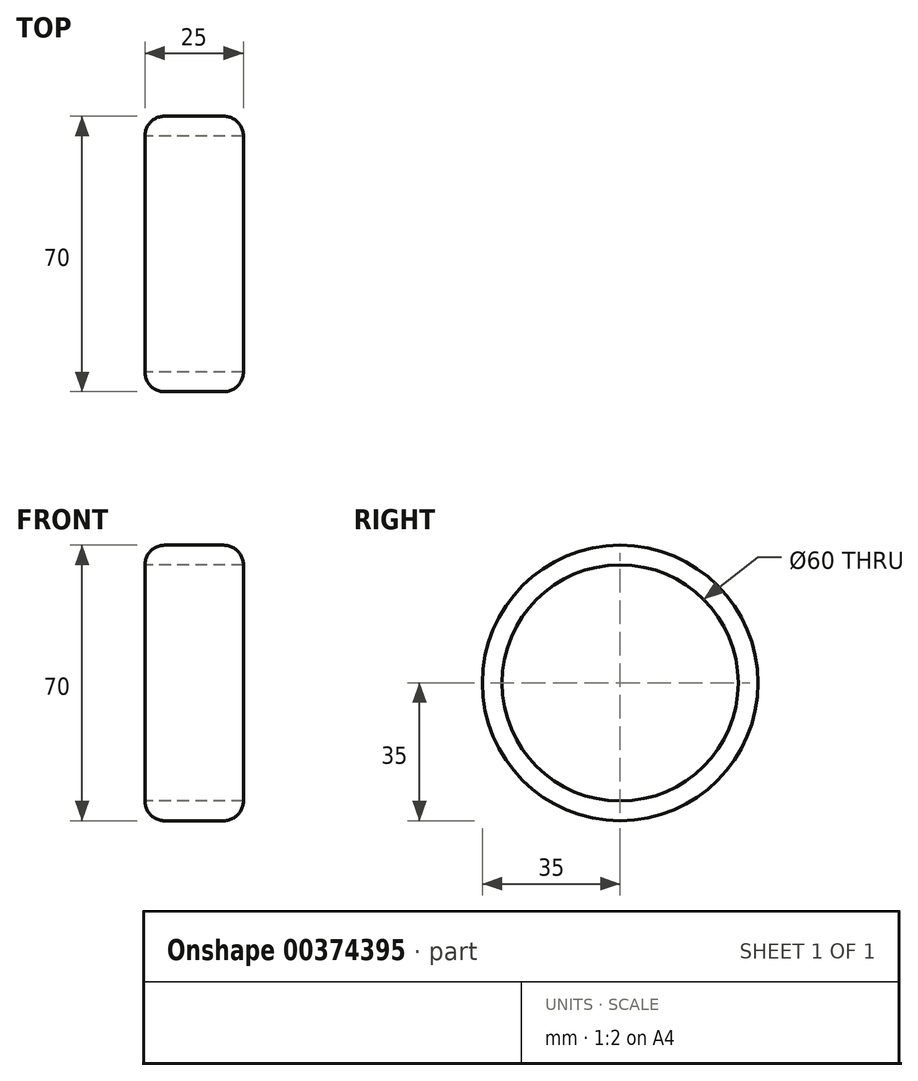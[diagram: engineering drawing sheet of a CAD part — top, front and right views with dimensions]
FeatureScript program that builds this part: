
annotation { "Feature Type Name" : "Feature", "Feature Type Description" : "" }
export const myFeature = defineFeature(function(context is Context, id is Id, definition is map)
    precondition{}
    {
        {
            var Q0;
            Q0=qCreatedBy(makeId("Right.planeOp"),FACE);
            var sketch = newSketch(context, id + "F0", { "sketchPlane" : qUnion([Q0])});
            skCircle(sketch, "E0", {"center": v(0, 0) * mm, "radius": 35 * mm});
            skCircle(sketch, "E1", {"center": v(0, 0) * mm, "radius": 30 * mm});
            skSolve(sketch);
        }
        {
            var Q0;
            Q0=makeQuery(id+"F0.imprint","IMPRINT",FACE,{"disambiguationData":[TD([[makeQuery(id+"F0.imprint","IMPRINT",EDGE,{"derivedFrom":sQuery(id+"F0.wireOp",EDGE,"E0")}),1.0]])]});
            extrude(context, id + "F1", {"entities" : qUnion([Q0]), "depth" : 25 * mm});
        }
        {
            var Q0;
            Q0=makeQuery(id+"F1.opExtrude","SWEPT_FACE",FACE,{"disambiguationData":[OSD([sQuery(id+"F0.wireOp",EDGE,"E0")])]});
            fillet(context, id + "F2", {"entities" : qUnion([Q0]), "radius" : 5 * mm, "tangentPropagation" : true, "allowEdgeOverflow" : false});
        }
    });
